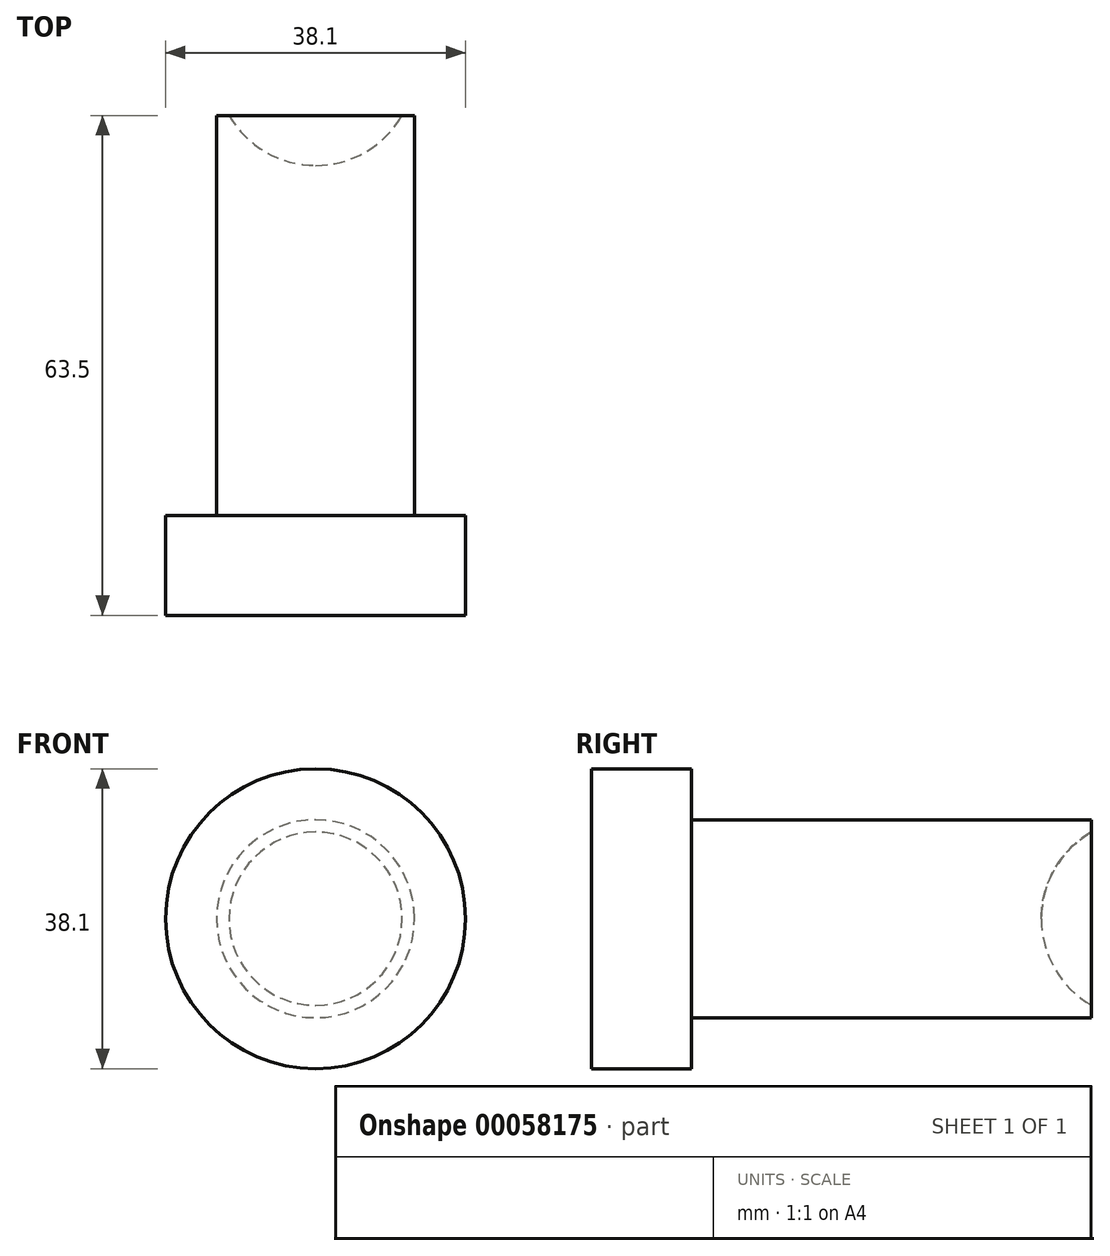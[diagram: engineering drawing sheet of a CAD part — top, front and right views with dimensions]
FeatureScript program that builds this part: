
annotation { "Feature Type Name" : "Feature", "Feature Type Description" : "" }
export const myFeature = defineFeature(function(context is Context, id is Id, definition is map)
    precondition{}
    {
        {
            var Q0;
            Q0=qCreatedBy(makeId("Front.planeOp"),FACE);
            var sketch = newSketch(context, id + "F0", { "sketchPlane" : qUnion([Q0])});
            skCircle(sketch, "E0", {"center": v(0, 0) * mm, "radius": 12.57 * mm});
            skSolve(sketch);
        }
        {
            var Q0;
            Q0=makeQuery(id+"F0.imprint","IMPRINT",FACE,{"disambiguationData":[TD([[makeQuery(id+"F0.imprint","IMPRINT",EDGE,{"derivedFrom":sQuery(id+"F0.wireOp",EDGE,"E0")}),1.0]])]});
            extrude(context, id + "F1", {"entities" : qUnion([Q0]), "oppositeDirection" : true, "depth" : 50.8 * mm});
        }
        {
            var Q0;
            Q0=qCreatedBy(makeId("Front.planeOp"),FACE);
            var sketch = newSketch(context, id + "F2", { "sketchPlane" : qUnion([Q0])});
            skCircle(sketch, "E1", {"center": v(0, 0) * mm, "radius": 19.05 * mm});
            skSolve(sketch);
        }
        {
            var Q0;
            Q0=makeQuery(id+"F2.imprint","IMPRINT",FACE,{"disambiguationData":[TD([[makeQuery(id+"F2.imprint","IMPRINT",EDGE,{"derivedFrom":sQuery(id+"F2.wireOp",EDGE,"E1")}),1.0]])]});
            extrude(context, id + "F3", {"entities" : qUnion([Q0]), "operationType" : NewBodyOperationType.ADD, "depth" : 12.7 * mm});
        }
        {
            var Q0;
            Q0=qCreatedBy(makeId("Right.planeOp"),FACE);
            var sketch = newSketch(context, id + "F4", { "sketchPlane" : qUnion([Q0])});
            skArc(sketch, "E2", {"start": v(69.85, 0) * mm, "mid": v(57.15, 12.7) * mm, "end": v(44.45, 0) * mm});
            skLineSegment(sketch, "E3", {"start": v(0, 0) * mm, "end": v(78.96, 0) * mm});
            skSolve(sketch);
        }
        {
            var Q0;
            {var subQ0=sQuery(id+"F4.wireOp",EDGE,"E2");Q0=makeQuery(id+"F4.imprint","IMPRINT",FACE,{"disambiguationData":[TD([[makeQuery(id+"F4.imprint","IMPRINT",EDGE,{"derivedFrom":subQ0}),1.0]])]});}
            var Q1;
            Q1=sQuery(id+"F4.wireOp",EDGE,"E2");
            var Q2;
            Q2=sQuery(id+"F4.wireOp",EDGE,"E3");
            revolve(context, id + "F5", {"operationType" : NewBodyOperationType.REMOVE, "entities" : qUnion([Q0]), "surfaceEntities" : qUnion([Q1]), "axis" : qUnion([Q2]), "revolveType" : RevolveType.FULL, "oppositeDirection" : true});
        }
    });
